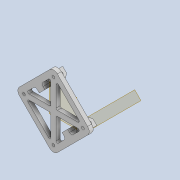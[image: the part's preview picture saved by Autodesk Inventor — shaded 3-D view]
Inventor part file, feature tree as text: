
AUTODESK INVENTOR PART (.ipt)
format: ipt  version: 2020 (Build 240168000, 168)  size: 279,040 bytes
history: native  units: mm
features: extrude x5, sketch x5, other x5, fillet x4, reference x4, projected_geometry x4, plane x2, chamfer x1
ambient origin geometry x8: Origin, YZ Plane, XZ Plane, XY Plane, X Axis, Y Axis, Z Axis, Center Point
bodies: Solid1 (feature_tree)
feature tree (30):
  plane  "Work Plane1"
  extrude  "Extrusion1"  Depth=40.0mm
  plane  "Work Plane2"
  extrude  "Extrusion2"  Depth=4.0mm
  extrude  "Extrusion3"  Depth=3.0mm
  extrude  "Extrusion4"  Depth=4.0mm
  fillet  "Fillet1"  Radius=6.0mm
  fillet  "Fillet2"  Radius=6.0mm
  chamfer  "Chamfer1"  Distance=6.0mm
  fillet  "Fillet3"  Radius=4.0mm
  extrude  "Extrusion5"  Depth=4.0mm TaperAngle=0.0deg
  fillet  "Fillet4"  Radius=8.0mm
  sketch  "Sketch1"  dims[d0=40.0mm d1=40.0mm]
  reference  "Reference1"
  reference  "Reference2"
  sketch  "Sketch2"  dims[d2=4.0mm d3=4.0mm]
  reference  "Reference3"
  reference  "Reference4"
  sketch  "Sketch3"  dims[d4=3.0mm d5=0.0mm d6=6.0mm]
  projected_geometry  "Projected Loop1"
  projected_geometry  "Projected Loop2"
  sketch  "Sketch4"  dims[d7=6.0mm d8=6.0mm d9=6.0mm d10=6.0mm d11=0.0mm d12=6.0mm d13=0.0mm d14=4.0mm]
  projected_geometry  "Projected Loop3"
  sketch  "Sketch5"  dims[d15=4.0mm d16=6.0mm d17=0.0mm d18=8.0mm d19=2.0mm d20=2.0mm d21=2.0mm d22=45.0deg d23=1.0mm d24=22.0mm d25=2.0mm d26=22.0mm d27=22.0mm d28=22.0mm d29=2.0mm d30=2.0mm d31=2.0mm d32=6.0mm d33=0.0mm d34=4.0mm]
  projected_geometry  "Projected Loop4"
  parser-record x1  (decoder bookkeeping rows leaked as tree rows — omitted from the tree; the rows remain in map.json)
  other  "tip_3_ass_base.iam"
  other  "mot_27_ass:1"
  other  "mot_27_2:1"
  other  "mot_test_enc_hh_1:1"
note: 1 file-system path scrubbed to <path> (originals preserved in map.json)
